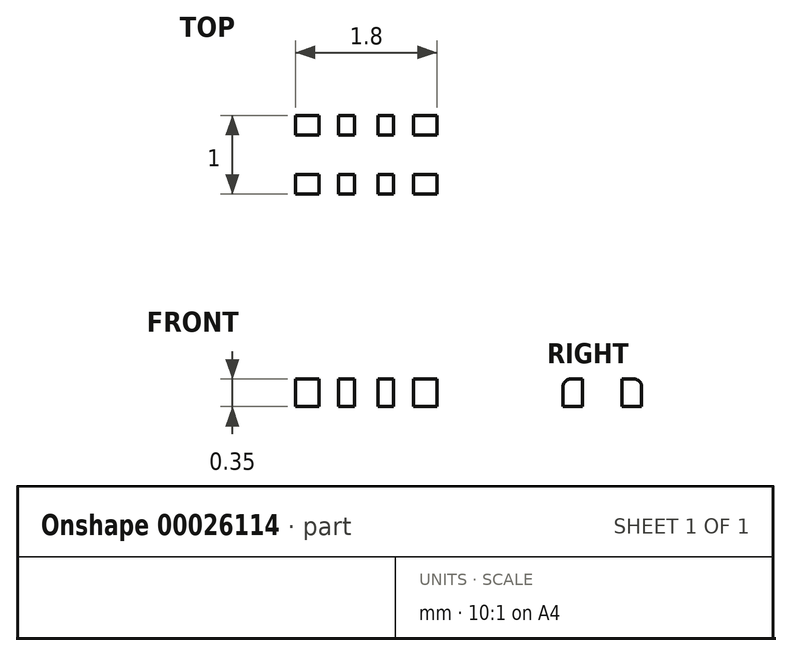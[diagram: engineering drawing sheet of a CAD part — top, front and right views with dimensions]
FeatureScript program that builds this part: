
annotation { "Feature Type Name" : "Feature", "Feature Type Description" : "" }
export const myFeature = defineFeature(function(context is Context, id is Id, definition is map)
    precondition{}
    {
        {
            var Q0;
            Q0=qCreatedBy(makeId("Top.planeOp"),FACE);
            var sketch = newSketch(context, id + "F0", { "sketchPlane" : qUnion([Q0])});
            skLineSegment(sketch, "E0.rect.bottom", {"start": v(1, -0.3) * mm, "end": v(-1, -0.3) * mm});
            skLineSegment(sketch, "E0.rect.top", {"start": v(1, 0.3) * mm, "end": v(-1, 0.3) * mm});
            skLineSegment(sketch, "E0.rect.left", {"start": v(1, -0.3) * mm, "end": v(1, 0.3) * mm});
            skLineSegment(sketch, "E0.rect.right", {"start": v(-1, -0.3) * mm, "end": v(-1, 0.3) * mm});
            skPoint(sketch, "E0.rect.middle", {"position": v(0, 0) * mm});
            skSolve(sketch);
        }
        {
            var Q0;
            Q0=makeQuery(id+"F0.imprint","IMPRINT",FACE,{"disambiguationData":[TD([[makeQuery(id+"F0.imprint","IMPRINT",EDGE,{"derivedFrom":sQuery(id+"F0.wireOp",EDGE,"E0.rect.bottom")}),-1.0]])]});
            extrude(context, id + "F1", {"entities" : qUnion([Q0]), "depth" : 0.35 * mm});
        }
        {
            var Q0;
            Q0=qCreatedBy(makeId("Top.planeOp"),FACE);
            var sketch = newSketch(context, id + "F2", { "sketchPlane" : qUnion([Q0])});
            skLineSegment(sketch, "E1.rect.bottom", {"start": v(-0.6, -0.5) * mm, "end": v(-0.9, -0.5) * mm});
            skLineSegment(sketch, "E1.rect.top", {"start": v(-0.6, -0.25) * mm, "end": v(-0.9, -0.25) * mm});
            skLineSegment(sketch, "E1.rect.left", {"start": v(-0.6, -0.5) * mm, "end": v(-0.6, -0.25) * mm});
            skLineSegment(sketch, "E1.rect.right", {"start": v(-0.9, -0.5) * mm, "end": v(-0.9, -0.25) * mm});
            skPoint(sketch, "E1.rect.middle", {"position": v(-0.75, -0.38) * mm});
            skLineSegment(sketch, "E2.MirrorCS", {"start": v(0.9, -0.5) * mm, "end": v(0.9, -0.25) * mm});
            skLineSegment(sketch, "E3.MirrorCS", {"start": v(0.6, -0.25) * mm, "end": v(0.9, -0.25) * mm});
            skLineSegment(sketch, "E4.MirrorCS", {"start": v(0.6, -0.5) * mm, "end": v(0.9, -0.5) * mm});
            skLineSegment(sketch, "E5.MirrorCS", {"start": v(0.6, -0.5) * mm, "end": v(0.6, -0.25) * mm});
            skLineSegment(sketch, "E6.MirrorCS", {"start": v(0.6, 0.25) * mm, "end": v(0.9, 0.25) * mm});
            skLineSegment(sketch, "E7.MirrorCS", {"start": v(0.6, 0.5) * mm, "end": v(0.6, 0.25) * mm});
            skLineSegment(sketch, "E8.MirrorCS", {"start": v(0.9, 0.5) * mm, "end": v(0.9, 0.25) * mm});
            skLineSegment(sketch, "E9.MirrorCS", {"start": v(0.6, 0.5) * mm, "end": v(0.9, 0.5) * mm});
            skLineSegment(sketch, "E10.MirrorCS", {"start": v(-0.9, 0.5) * mm, "end": v(-0.9, 0.25) * mm});
            skLineSegment(sketch, "E11.MirrorCS", {"start": v(-0.6, 0.25) * mm, "end": v(-0.9, 0.25) * mm});
            skLineSegment(sketch, "E12.MirrorCS", {"start": v(-0.6, 0.5) * mm, "end": v(-0.6, 0.25) * mm});
            skLineSegment(sketch, "E13.MirrorCS", {"start": v(-0.6, 0.5) * mm, "end": v(-0.9, 0.5) * mm});
            skLineSegment(sketch, "E14.rect.bottom", {"start": v(-0.15, 0.25) * mm, "end": v(-0.35, 0.25) * mm});
            skLineSegment(sketch, "E14.rect.top", {"start": v(-0.15, 0.5) * mm, "end": v(-0.35, 0.5) * mm});
            skLineSegment(sketch, "E14.rect.left", {"start": v(-0.15, 0.25) * mm, "end": v(-0.15, 0.5) * mm});
            skLineSegment(sketch, "E14.rect.right", {"start": v(-0.35, 0.25) * mm, "end": v(-0.35, 0.5) * mm});
            skPoint(sketch, "E14.rect.middle", {"position": v(-0.25, 0.38) * mm});
            skLineSegment(sketch, "E15.MirrorCS", {"start": v(0.15, 0.25) * mm, "end": v(0.15, 0.5) * mm});
            skLineSegment(sketch, "E16.MirrorCS", {"start": v(0.15, 0.5) * mm, "end": v(0.35, 0.5) * mm});
            skLineSegment(sketch, "E17.MirrorCS", {"start": v(0.35, 0.25) * mm, "end": v(0.35, 0.5) * mm});
            skLineSegment(sketch, "E18.MirrorCS", {"start": v(0.15, 0.25) * mm, "end": v(0.35, 0.25) * mm});
            skLineSegment(sketch, "E19.MirrorCS", {"start": v(-0.35, -0.25) * mm, "end": v(-0.35, -0.5) * mm});
            skLineSegment(sketch, "E20.MirrorCS", {"start": v(-0.15, -0.25) * mm, "end": v(-0.35, -0.25) * mm});
            skLineSegment(sketch, "E21.MirrorCS", {"start": v(-0.15, -0.25) * mm, "end": v(-0.15, -0.5) * mm});
            skLineSegment(sketch, "E22.MirrorCS", {"start": v(-0.15, -0.5) * mm, "end": v(-0.35, -0.5) * mm});
            skLineSegment(sketch, "E23.MirrorCS", {"start": v(0.15, -0.5) * mm, "end": v(0.35, -0.5) * mm});
            skLineSegment(sketch, "E24.MirrorCS", {"start": v(0.15, -0.25) * mm, "end": v(0.15, -0.5) * mm});
            skLineSegment(sketch, "E25.MirrorCS", {"start": v(0.15, -0.25) * mm, "end": v(0.35, -0.25) * mm});
            skLineSegment(sketch, "E26.MirrorCS", {"start": v(0.35, -0.25) * mm, "end": v(0.35, -0.5) * mm});
            skSolve(sketch);
        }
        {
            var Q0;
            Q0=qSketchRegion(id+"F2",true);
            extrude(context, id + "F3", {"entities" : qUnion([Q0]), "depth" : 0.35 * mm});
        }
        {
            var Q0;
            Q0=makeQuery(id+"F3.opExtrude","CAP_EDGE",EDGE,{"disambiguationData":[OSD([sQuery(id+"F2.wireOp",EDGE,"E9.MirrorCS")])],"isStart":false});
            var Q1;
            Q1=makeQuery(id+"F3.opExtrude","CAP_EDGE",EDGE,{"disambiguationData":[OSD([sQuery(id+"F2.wireOp",EDGE,"E16.MirrorCS")])],"isStart":false});
            var Q2;
            Q2=makeQuery(id+"F3.opExtrude","CAP_EDGE",EDGE,{"disambiguationData":[OSD([sQuery(id+"F2.wireOp",EDGE,"E14.rect.top")])],"isStart":false});
            var Q3;
            Q3=makeQuery(id+"F3.opExtrude","CAP_EDGE",EDGE,{"disambiguationData":[OSD([sQuery(id+"F2.wireOp",EDGE,"E13.MirrorCS")])],"isStart":false});
            var Q4;
            Q4=makeQuery(id+"F3.opExtrude","CAP_EDGE",EDGE,{"disambiguationData":[OSD([sQuery(id+"F2.wireOp",EDGE,"E4.MirrorCS")])],"isStart":false});
            var Q5;
            Q5=makeQuery(id+"F3.opExtrude","CAP_EDGE",EDGE,{"disambiguationData":[OSD([sQuery(id+"F2.wireOp",EDGE,"E23.MirrorCS")])],"isStart":false});
            var Q6;
            Q6=makeQuery(id+"F3.opExtrude","CAP_EDGE",EDGE,{"disambiguationData":[OSD([sQuery(id+"F2.wireOp",EDGE,"E22.MirrorCS")])],"isStart":false});
            var Q7;
            Q7=makeQuery(id+"F3.opExtrude","CAP_EDGE",EDGE,{"disambiguationData":[OSD([sQuery(id+"F2.wireOp",EDGE,"E1.rect.bottom")])],"isStart":false});
            fillet(context, id + "F4", {"entities" : qUnion([Q0, Q1, Q2, Q3, Q4, Q5, Q6, Q7]), "radius" : 0.1 * mm, "tangentPropagation" : true, "allowEdgeOverflow" : false});
        }
        {
            var Q0;
            Q0=makeQuery(id+"F3.opExtrude","SWEPT_BODY",BODY,{"disambiguationData":[OSD([sQuery(id+"F2.wireOp",EDGE,"E1.rect.bottom"),sQuery(id+"F2.wireOp",EDGE,"E1.rect.top"),sQuery(id+"F2.wireOp",EDGE,"E1.rect.left"),sQuery(id+"F2.wireOp",EDGE,"E1.rect.right")])]});
            var Q1;
            Q1=makeQuery(id+"F1.opExtrude","SWEPT_BODY",BODY,{"disambiguationData":[OSD([sQuery(id+"F0.wireOp",EDGE,"E0.rect.bottom"),sQuery(id+"F0.wireOp",EDGE,"E0.rect.top"),sQuery(id+"F0.wireOp",EDGE,"E0.rect.left"),sQuery(id+"F0.wireOp",EDGE,"E0.rect.right")])]});
            booleanBodies(context, id + "F5", {"operationType" : BooleanOperationType.SUBTRACTION, "tools" : qUnion([Q0]), "targets" : qUnion([Q1]), "keepTools" : true});
        }
        {
            var Q0;
            Q0=makeQuery(id+"F3.opExtrude","SWEPT_BODY",BODY,{"disambiguationData":[OSD([sQuery(id+"F2.wireOp",EDGE,"E2.MirrorCS"),sQuery(id+"F2.wireOp",EDGE,"E3.MirrorCS"),sQuery(id+"F2.wireOp",EDGE,"E4.MirrorCS"),sQuery(id+"F2.wireOp",EDGE,"E5.MirrorCS")])]});
            var Q1;
            Q1=makeQuery(id+"F3.opExtrude","SWEPT_BODY",BODY,{"disambiguationData":[OSD([sQuery(id+"F2.wireOp",EDGE,"E6.MirrorCS"),sQuery(id+"F2.wireOp",EDGE,"E7.MirrorCS"),sQuery(id+"F2.wireOp",EDGE,"E8.MirrorCS"),sQuery(id+"F2.wireOp",EDGE,"E9.MirrorCS")])]});
            var Q2;
            Q2=makeQuery(id+"F3.opExtrude","SWEPT_BODY",BODY,{"disambiguationData":[OSD([sQuery(id+"F2.wireOp",EDGE,"E10.MirrorCS"),sQuery(id+"F2.wireOp",EDGE,"E11.MirrorCS"),sQuery(id+"F2.wireOp",EDGE,"E12.MirrorCS"),sQuery(id+"F2.wireOp",EDGE,"E13.MirrorCS")])]});
            var Q3;
            Q3=makeQuery(id+"F3.opExtrude","SWEPT_BODY",BODY,{"disambiguationData":[OSD([sQuery(id+"F2.wireOp",EDGE,"E14.rect.bottom"),sQuery(id+"F2.wireOp",EDGE,"E14.rect.top"),sQuery(id+"F2.wireOp",EDGE,"E14.rect.left"),sQuery(id+"F2.wireOp",EDGE,"E14.rect.right")])]});
            var Q4;
            Q4=makeQuery(id+"F3.opExtrude","SWEPT_BODY",BODY,{"disambiguationData":[OSD([sQuery(id+"F2.wireOp",EDGE,"E15.MirrorCS"),sQuery(id+"F2.wireOp",EDGE,"E16.MirrorCS"),sQuery(id+"F2.wireOp",EDGE,"E17.MirrorCS"),sQuery(id+"F2.wireOp",EDGE,"E18.MirrorCS")])]});
            var Q5;
            Q5=makeQuery(id+"F3.opExtrude","SWEPT_BODY",BODY,{"disambiguationData":[OSD([sQuery(id+"F2.wireOp",EDGE,"E19.MirrorCS"),sQuery(id+"F2.wireOp",EDGE,"E20.MirrorCS"),sQuery(id+"F2.wireOp",EDGE,"E21.MirrorCS"),sQuery(id+"F2.wireOp",EDGE,"E22.MirrorCS")])]});
            var Q6;
            Q6=makeQuery(id+"F3.opExtrude","SWEPT_BODY",BODY,{"disambiguationData":[OSD([sQuery(id+"F2.wireOp",EDGE,"E23.MirrorCS"),sQuery(id+"F2.wireOp",EDGE,"E24.MirrorCS"),sQuery(id+"F2.wireOp",EDGE,"E25.MirrorCS"),sQuery(id+"F2.wireOp",EDGE,"E26.MirrorCS")])]});
            var Q7;
            Q7=makeQuery(id+"F1.opExtrude","SWEPT_BODY",BODY,{"disambiguationData":[OSD([sQuery(id+"F0.wireOp",EDGE,"E0.rect.bottom"),sQuery(id+"F0.wireOp",EDGE,"E0.rect.top"),sQuery(id+"F0.wireOp",EDGE,"E0.rect.left"),sQuery(id+"F0.wireOp",EDGE,"E0.rect.right")])]});
            booleanBodies(context, id + "F6", {"operationType" : BooleanOperationType.SUBTRACTION, "tools" : qUnion([Q0, Q1, Q2, Q3, Q4, Q5, Q6]), "targets" : qUnion([Q7]), "keepTools" : true});
        }
        {
            var Q0;
            Q0=makeQuery(id+"F1.opExtrude","SWEPT_BODY",BODY,{"disambiguationData":[OSD([sQuery(id+"F0.wireOp",EDGE,"E0.rect.bottom"),sQuery(id+"F0.wireOp",EDGE,"E0.rect.top"),sQuery(id+"F0.wireOp",EDGE,"E0.rect.left"),sQuery(id+"F0.wireOp",EDGE,"E0.rect.right")])]});
            deleteBodies(context, id + "F7", {"entities" : qUnion([Q0])});
        }
    });
